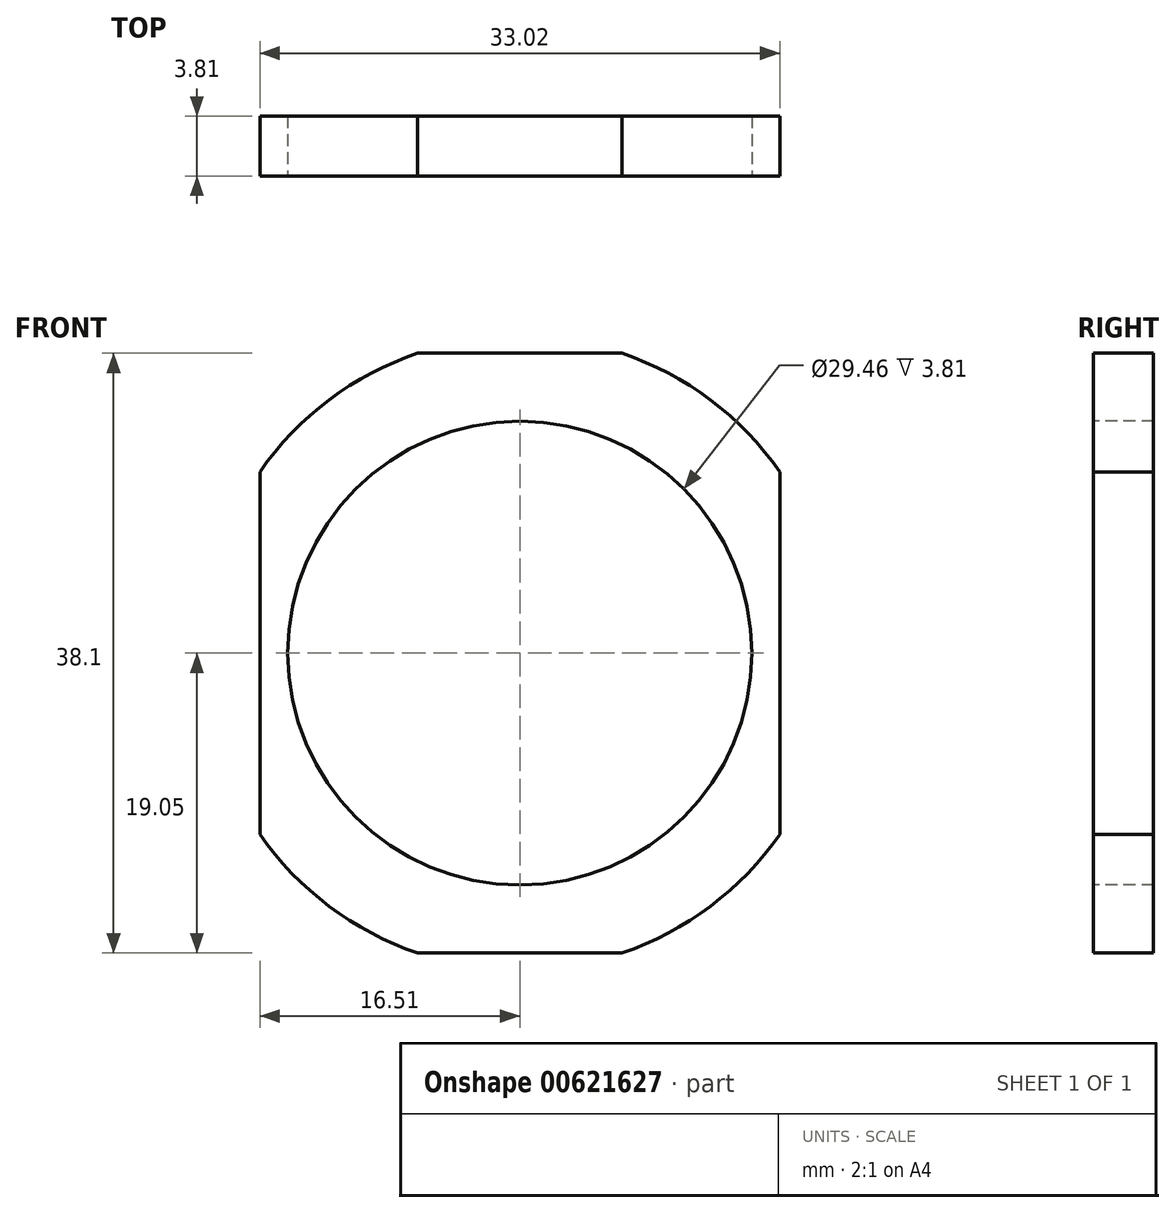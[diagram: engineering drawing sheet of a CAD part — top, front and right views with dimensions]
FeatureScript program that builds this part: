
annotation { "Feature Type Name" : "Feature", "Feature Type Description" : "" }
export const myFeature = defineFeature(function(context is Context, id is Id, definition is map)
    precondition{}
    {
        {
            var Q0;
            Q0=qCreatedBy(makeId("Front.planeOp"),FACE);
            var sketch = newSketch(context, id + "F0", { "sketchPlane" : qUnion([Q0])});
            skLineSegment(sketch, "E0.bottom", {"start": v(16.51, 19.05) * mm, "end": v(-16.5, 19.05) * mm});
            skLineSegment(sketch, "E0.top", {"start": v(16.5, -19.05) * mm, "end": v(-16.51, -19.05) * mm});
            skLineSegment(sketch, "E0.left", {"start": v(16.51, 19.05) * mm, "end": v(16.5, -19.05) * mm});
            skLineSegment(sketch, "E0.right", {"start": v(-16.5, 19.05) * mm, "end": v(-16.51, -19.05) * mm});
            skPoint(sketch, "E0.middle", {"position": v(0, 0) * mm});
            skSolve(sketch);
        }
        {
            var Q0;
            Q0 = qSketchRegion(id + "F0", true);
            extrude(context, id + "F1", {"entities" : qUnion([Q0]), "depth" : 3.8 * mm, "offsetDistance" : 25.4 * mm});
        }
        {
            var Q0;
            Q0=makeQuery(id+"F1.opExtrude","CAP_FACE",FACE,{"disambiguationData":[OSD([sQuery(id+"F0.wireOp",EDGE,"E0.bottom"),sQuery(id+"F0.wireOp",EDGE,"E0.top"),sQuery(id+"F0.wireOp",EDGE,"E0.left"),sQuery(id+"F0.wireOp",EDGE,"E0.right")])],"isStart":false});
            var sketch = newSketch(context, id + "F2", { "sketchPlane" : qUnion([Q0])});
            skCircle(sketch, "E1", {"center": v(0, 0) * mm, "radius": 14.73 * mm});
            skCircle(sketch, "E2", {"center": v(0, 0) * mm, "radius": 25.2 * mm});
            skCircle(sketch, "E3", {"center": v(0, 0) * mm, "radius": 20.13 * mm});
            skSolve(sketch);
        }
        {
            var Q0;
            Q0 = qSketchRegion(id + "F2", true);
            extrude(context, id + "F3", {"entities" : qUnion([Q0]), "operationType" : NewBodyOperationType.REMOVE, "oppositeDirection" : true, "depth" : 25.4 * mm, "offsetDistance" : 25.4 * mm});
        }
        {
            var Q0;
            Q0=makeQuery(id+"F1.opExtrude","CAP_FACE",FACE,{"disambiguationData":[OSD([sQuery(id+"F0.wireOp",EDGE,"E0.bottom"),sQuery(id+"F0.wireOp",EDGE,"E0.top"),sQuery(id+"F0.wireOp",EDGE,"E0.left"),sQuery(id+"F0.wireOp",EDGE,"E0.right")])],"isStart":false});
            var sketch = newSketch(context, id + "F4", { "sketchPlane" : qUnion([Q0])});
            skCircle(sketch, "E4", {"center": v(0, 0) * mm, "radius": 14.73 * mm});
            skSolve(sketch);
        }
        {
            var Q0;
            Q0 = qSketchRegion(id + "F4", true);
            extrude(context, id + "F5", {"entities" : qUnion([Q0]), "operationType" : NewBodyOperationType.REMOVE, "oppositeDirection" : true, "depth" : 25.4 * mm, "offsetDistance" : 25.4 * mm});
        }
    });
